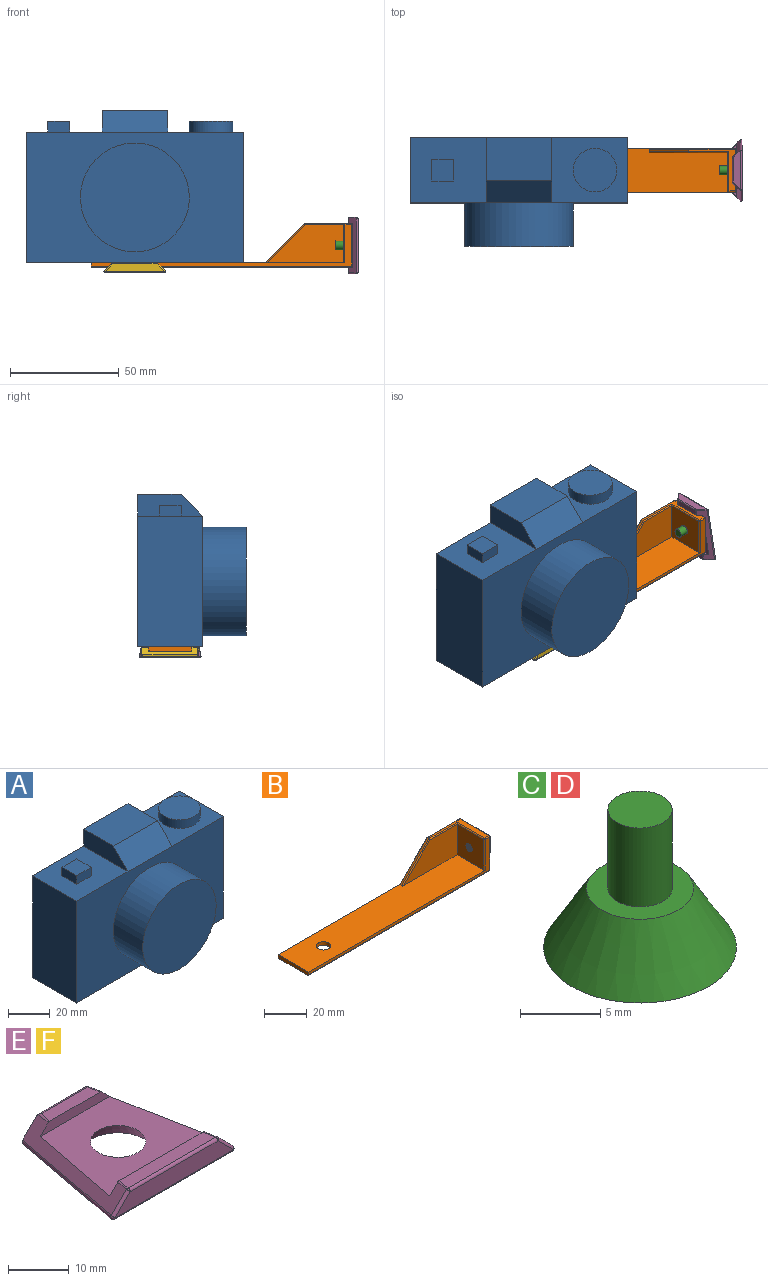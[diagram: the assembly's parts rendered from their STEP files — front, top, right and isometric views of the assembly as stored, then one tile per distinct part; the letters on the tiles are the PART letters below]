
ASSEMBLY  parts=6 mates=6
PART A: 20 faces, bbox 100x50x70 mm
  f0: plane 30x10mm, normal (1,0,0), area 250mm2, adj f1,f4,f9,f10
  f1: plane 30x20mm, normal (0,0,1), area 600mm2, adj f0,f2,f9,f10
  f2: plane 30x10mm, normal (-1,0,0), area 250mm2, adj f1,f3,f9,f10
  f3: plane 35x30mm, normal (0,0,1), area 950mm2, adj f2,f5,f8,f9,f13,f14,f15,f16
  f4: plane 35x30mm, normal (0,0,1), area 735.8mm2, adj f0,f7,f8,f9,f11
  f5: plane 60x30mm, normal (-1,0,0), area 1800mm2, adj f3,f6,f8,f9
  f6: plane 100x30mm, normal (0,0,-1), area 3000mm2, adj f5,f7,f8,f9
  f7: plane 60x30mm, normal (1,0,0), area 1800mm2, adj f4,f6,f8,f9
  f8: plane 100x60mm, normal (0,-1,0), area 4036.5mm2, adj f3,f4,f5,f6,f7,f10,f18
  f9: plane 100x70mm, normal (0,1,0), area 6300mm2, adj f0,f1,f2,f3,f4,f5,f6,f7
  f10: plane 30x10mm, normal (0,-0.71,0.71), area 424.3mm2, adj f0,f1,f2,f8
  f11: cylinder r=10mm len=20mm, axis (0,0,-1), area 314.2mm2, adj f4,f12
  f12: plane 20x20mm, normal (0,0,1), area 314.2mm2, adj f11
  f13: plane 10x5mm, normal (0,1,0), area 50mm2, adj f3,f14,f16,f17
  f14: plane 10x5mm, normal (-1,0,0), area 50mm2, adj f3,f13,f15,f17
  f15: plane 10x5mm, normal (0,-1,0), area 50mm2, adj f3,f14,f16,f17
  f16: plane 10x5mm, normal (1,0,0), area 50mm2, adj f3,f13,f15,f17
  f17: plane 10x10mm, normal (0,0,1), area 100mm2, adj f13,f14,f15,f16
  f18: cylinder r=25mm len=50mm, axis (0,1,0), area 3141.6mm2, adj f8,f19
  f19: plane 50x50mm, normal (0,-1,0), area 1963.5mm2, adj f18
PART B: 34 faces, bbox 120.2x20.2x20.2 mm
  f0: cylinder r=2mm len=4mm, axis (1,0,0), area 17.8mm2, adj f9,f12,f13,f14,f15
  f1: plane 116.71x20.21mm, normal (0,0,1), area 2213.2mm2, adj f2,f4,f6,f7,f8,f9,f11,f16
  f2: plane 119.5x19mm, normal (0,-1,0), area 231.8mm2, adj f1,f6,f18,f19,f25,f26
  f3: plane 119.5x19mm, normal (0,0,-1), area 2235.5mm2, adj f6,f7,f18,f23,f24
  f4: plane 119.5x19mm, normal (0,1,0), area 705mm2, adj f1,f6,f23,f29,f32,f33
  f5: plane 19x19mm, normal (1,0,0), area 341.4mm2, adj f12,f24,f25,f29,f30
  f6: plane 20x2mm, normal (-1,0,0), area 39.9mm2, adj f1,f2,f3,f4,f18,f23
  f7: cylinder r=3.34mm len=6.68mm, axis (0,0,1), area 42mm2, adj f1,f3
  f8: plane 35.29x17.5mm, normal (0,-1,0), area 464.5mm2, adj f1,f9,f16,f17
  f9: plane 17.5x17.5mm, normal (-1,0,0), area 293.7mm2, adj f0,f1,f8,f19,f20
  f10: plane 21.5x19mm, normal (0,0,1), area 75.5mm2, adj f11,f17,f20,f26,f30,f32
  f11: plane 18x18mm, normal (-0.71,0,0.71), area 25.5mm2, adj f1,f10,f16,f33
  f12: cone r=2mm half-angle=45deg, axis (1,0,0), area 8.5mm2, adj f0,f5,f13,f14
  f13: bspline ~4.53x4.52mm, area 27.6mm2, adj f0,f12,f14,f15
  f14: bspline ~5.23x4.53mm, area 28.6mm2, adj f0,f12,f13,f15
  f15: plane 0.32x0.28mm, normal (0,0,1), area 0mm2, adj f0,f13,f14
  f16: cylinder r=0.5mm len=18.35mm, axis (-0.71,0,-0.71), area 19.7mm2, adj f1,f8,f11,f17
  f17: cylinder r=0.5mm len=18.5mm, axis (-1,0,0), area 14.3mm2, adj f8,f10,f16,f20
  f18: cylinder r=0.5mm len=119.5mm, axis (-1,0,0), area 93.9mm2, adj f2,f3,f6,f21
  f19: cylinder r=0.5mm len=17.5mm, axis (0,0,-1), area 13.7mm2, adj f1,f2,f9,f22
  f20: cylinder r=0.5mm len=18mm, axis (0,1,0), area 13.9mm2, adj f9,f10,f17,f22
  f21: sphere r=0.5mm, area 0.4mm2, adj f18,f24,f25
  f22: sphere r=0.5mm, area 0.4mm2, adj f19,f20,f26
  f23: cylinder r=0.5mm len=119.5mm, axis (1,0,0), area 93.9mm2, adj f3,f4,f6,f27
  f24: cylinder r=0.5mm len=19mm, axis (0,-1,0), area 14.9mm2, adj f3,f5,f21,f27
  f25: cylinder r=0.5mm len=19mm, axis (0,0,1), area 14.9mm2, adj f2,f5,f21,f28
  f26: cylinder r=0.5mm len=3mm, axis (1,0,0), area 2.4mm2, adj f2,f10,f22,f28
  f27: sphere r=0.5mm, area 0.2mm2, adj f23,f24,f29
  f28: sphere r=0.5mm, area 0.4mm2, adj f25,f26,f30
  f29: cylinder r=0.5mm len=19mm, axis (0,0,-1), area 14.9mm2, adj f4,f5,f27,f31
  f30: cylinder r=0.5mm len=19mm, axis (0,1,0), area 14.9mm2, adj f5,f10,f28,f31
  f31: sphere r=0.5mm, area 0.2mm2, adj f29,f30,f32
  f32: cylinder r=0.5mm len=21.5mm, axis (-1,0,0), area 16.8mm2, adj f4,f10,f31,f33
  f33: cylinder r=0.5mm len=18.35mm, axis (0.71,0,0.71), area 19.7mm2, adj f1,f4,f11,f32
PART C: 5 faces, bbox 12x12x10.5 mm
  f0: plane 12x12mm, normal (0,0,-1), area 113.1mm2, adj f2
  f1: plane 6.68x6.68mm, normal (0,0,1), area 22.5mm2, adj f2,f3
  f2: cone r=6mm half-angle=30.6deg, axis (0,0,-1), area 153.4mm2, adj f0,f1
  f3: cylinder r=2mm len=6mm, axis (0,0,-1), area 75.4mm2, adj f1,f4
  f4: plane 4x4mm, normal (0,0,1), area 12.6mm2, adj f3
PART D: same geometry as C
PART E: 30 faces, bbox 28.4x26x4.5 mm
  f0: plane 11.73x2.5mm, normal (0,0,1), area 28.1mm2, adj f10,f24,f26,f29
  f1: plane 27.38x25mm, normal (0,0,-1), area 451.2mm2, adj f7,f18,f20,f22,f23
  f2: plane 20.38x2.5mm, normal (0,0,1), area 49.7mm2, adj f9,f11,f13,f14
  f3: plane 27.38x3.5mm, normal (0,-1,0), area 83.6mm2, adj f13,f15,f18,f19
  f4: plane 25x8.31mm, normal (0.7,0.13,0.7), area 72.1mm2, adj f8,f9,f10,f14,f19,f23,f27,f29
  f5: plane 18.19x3.51mm, normal (0,1,0), area 52.1mm2, adj f6,f20,f22,f26,f27
  f6: plane 25.43x8.36mm, normal (-0.7,0.13,0.7), area 74.2mm2, adj f5,f8,f9,f10,f11,f15,f20,f24
  f7: cone r=6mm half-angle=30.6deg, axis (0,0,-1), area 96mm2, adj f1,f8
  f8: plane 23.85x20mm, normal (0,0,1), area 335.8mm2, adj f4,f6,f7,f9,f10
  f9: plane 23.85x2.01mm, normal (0,1,0), area 43.7mm2, adj f2,f4,f6,f8,f11,f14
  f10: plane 16.16x2.01mm, normal (0,-1,0), area 28.3mm2, adj f0,f4,f6,f8,f24,f29
  f11: cylinder r=0.5mm len=2.57mm, axis (0.19,0.98,0), area 1mm2, adj f2,f6,f9,f12
  f12: sphere r=0.5mm, area 0.2mm2, adj f11,f13,f15
  f13: cylinder r=0.5mm len=20.38mm, axis (1,0,0), area 16mm2, adj f2,f3,f12,f16
  f14: cylinder r=0.5mm len=2.57mm, axis (-0.19,0.98,0), area 1mm2, adj f2,f4,f9,f16
  f15: cylinder r=0.5mm len=3.85mm, axis (-0.71,0,-0.71), area 4.2mm2, adj f3,f6,f12,f17
  f16: sphere r=0.5mm, area 0.2mm2, adj f13,f14,f19
  f17: sphere r=0.5mm, area 0.7mm2, adj f15,f18,f20
  f18: cylinder r=0.5mm len=27.38mm, axis (-1,0,0), area 21.5mm2, adj f1,f3,f17,f21
  f19: cylinder r=0.5mm len=3.85mm, axis (-0.71,0,0.71), area 4.2mm2, adj f3,f4,f16,f21
  f20: cylinder r=0.5mm len=25.53mm, axis (-0.19,-0.98,0), area 30.2mm2, adj f1,f5,f6,f17,f22
  f21: sphere r=0.5mm, area 0.7mm2, adj f18,f19,f23
  f22: cylinder r=0.5mm len=18.18mm, axis (-1,0,0), area 14.2mm2, adj f1,f5,f20,f25
  f23: cylinder r=0.5mm len=25.09mm, axis (0.19,-0.98,0), area 29.9mm2, adj f1,f4,f21,f25
  f24: cylinder r=0.5mm len=2.92mm, axis (0.19,0.98,0), area 1.1mm2, adj f0,f6,f10,f26
  f25: sphere r=0.5mm, area 0.5mm2, adj f22,f23,f27
  f26: cylinder r=0.5mm len=11.38mm, axis (1,0,0), area 8.7mm2, adj f0,f5,f6,f24,f28
  f27: cylinder r=0.5mm len=3.85mm, axis (0.71,0,-0.71), area 3.6mm2, adj f4,f5,f25,f28
  f28: sphere r=0.5mm, area 0.2mm2, adj f26,f27,f29
  f29: cylinder r=0.5mm len=2.63mm, axis (-0.19,0.98,0), area 1mm2, adj f0,f4,f10,f28
PART F: same geometry as E
PLACE A t=(7.04,-31.41,-20.99)mm
PLACE B t=(13.45,-46.41,-51.06)mm
PLACE C rot(axis=(-0.71,0,0.71),180deg) t=(115.95,-46.41,-38.56)mm
PLACE D t=(13.45,-46.41,-51.06)mm
PLACE E rot(axis=(0.58,-0.58,-0.58),120deg) t=(115.95,-46.41,-38.56)mm
PLACE F t=(13.45,-46.41,-51.06)mm
MATE fastened D.f2 <-> F.f7  axis (0,0,-1) through (13.45,-46.41,-51.06)mm
MATE fastened E.f7 <-> B.f0  axis (-1,0,0) through (113.45,-46.41,-38.56)mm
MATE fastened A.f6 <-> D.f3  axis (0,0,-1) through (13.45,-46.41,-46.56)mm
MATE planar A.f6 <-> B.f7  axis (0,0,-1) through (13.45,-46.41,-46.56)mm
MATE fastened F.f7 <-> B.f7  axis (0,0,1) through (13.45,-46.41,-48.56)mm
MATE fastened C.f2 <-> E.f7  axis (1,0,0) through (115.95,-46.41,-38.56)mm
